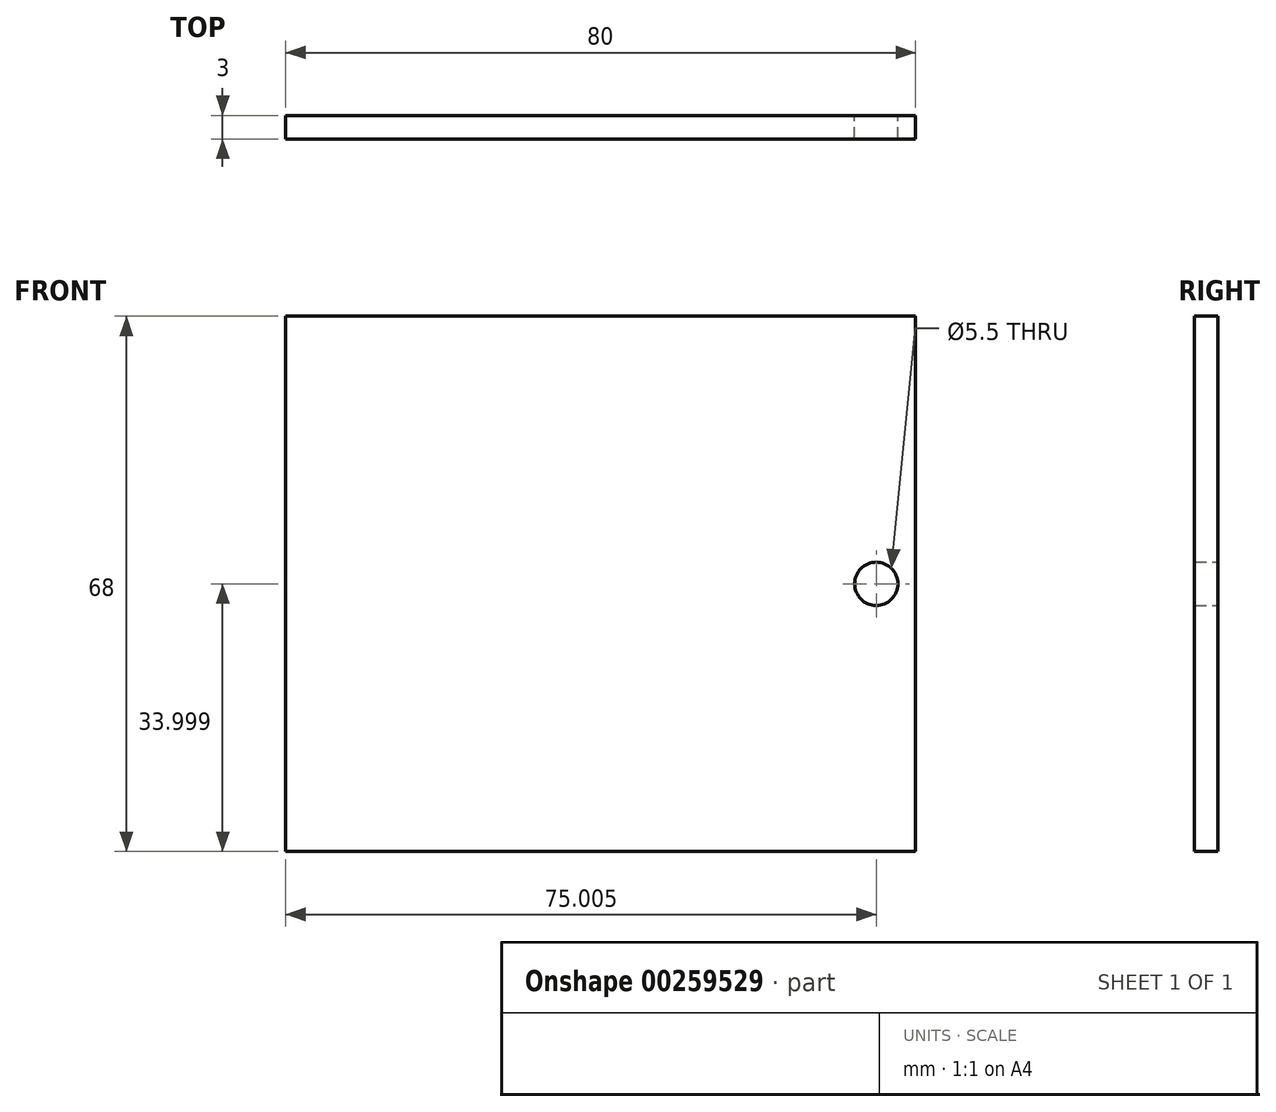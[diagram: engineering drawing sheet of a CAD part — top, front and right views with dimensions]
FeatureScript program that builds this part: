
annotation { "Feature Type Name" : "Feature", "Feature Type Description" : "" }
export const myFeature = defineFeature(function(context is Context, id is Id, definition is map)
    precondition{}
    {
        {
            var Q0;
            Q0=qCreatedBy(makeId("Front.planeOp"),FACE);
            var sketch = newSketch(context, id + "F0", { "sketchPlane" : qUnion([Q0])});
            skLineSegment(sketch, "E0.bottom", {"start": v(-85.67, 74.8) * mm, "end": v(-5.67, 74.8) * mm});
            skLineSegment(sketch, "E0.top", {"start": v(-85.67, 6.8) * mm, "end": v(-5.67, 6.8) * mm});
            skLineSegment(sketch, "E0.left", {"start": v(-85.67, 74.8) * mm, "end": v(-85.67, 6.8) * mm});
            skLineSegment(sketch, "E0.right", {"start": v(-5.67, 74.8) * mm, "end": v(-5.67, 6.8) * mm});
            skLineSegment(sketch, "E1", {"start": v(-5.67, 40.8) * mm, "end": v(-85.67, 40.8) * mm, "construction": true});
            skCircle(sketch, "E2", {"center": v(-10.67, 40.8) * mm, "radius": 2.75 * mm});
            skSolve(sketch);
        }
        {
            var Q0;
            Q0 = qSketchRegion(id + "F0", true);
            extrude(context, id + "F1", {"entities" : qUnion([Q0]), "depth" : 3 * mm});
        }
        {
            var Q0;
            Q0=makeQuery(id+"F1.opExtrude","SWEPT_FACE",FACE,{"disambiguationData":[OSD([sQuery(id+"F0.wireOp",EDGE,"E0.right")])]});
            var sketch = newSketch(context, id + "F2", { "sketchPlane" : qUnion([Q0])});
            skLineSegment(sketch, "E3", {"start": v(-3, 40.8) * mm, "end": v(0, 40.8) * mm});
            skSolve(sketch);
        }
        {
            var Q0;
            Q0=makeQuery(id+"F1.opExtrude","SWEPT_BODY",BODY,{"disambiguationData":[OSD([sQuery(id+"F0.wireOp",EDGE,"E0.bottom"),sQuery(id+"F0.wireOp",EDGE,"E0.top"),sQuery(id+"F0.wireOp",EDGE,"E0.left"),sQuery(id+"F0.wireOp",EDGE,"E0.right"),sQuery(id+"F0.wireOp",EDGE,"E2")])]});
            var Q1;
            Q1=sQuery(id+"F2.wireOp",EDGE,"E3");
            transform(context, id + "F3", {"entities" : qUnion([Q0]), "transformType" : TransformType.ROTATION, "transformAxis" : qUnion([Q1]), "angle" : 180 * degree, "makeCopy" : true});
        }
        {
            var Q0;
            Q0=makeQuery(id+"F3.opPattern","COPY",BODY,{"derivedFrom":makeQuery(id+"F1.opExtrude","SWEPT_BODY",BODY,{"disambiguationData":[OSD([sQuery(id+"F0.wireOp",EDGE,"E0.bottom"),sQuery(id+"F0.wireOp",EDGE,"E0.top"),sQuery(id+"F0.wireOp",EDGE,"E0.left"),sQuery(id+"F0.wireOp",EDGE,"E0.right"),sQuery(id+"F0.wireOp",EDGE,"E2")])]}),"instanceName":"1"});
            deleteBodies(context, id + "F4", {"entities" : qUnion([Q0])});
        }
    });
